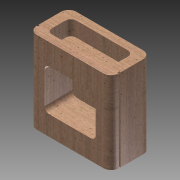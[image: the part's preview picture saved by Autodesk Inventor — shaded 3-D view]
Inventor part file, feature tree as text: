
AUTODESK INVENTOR PART (.ipt)
format: ipt  version: 2015 (Build 190159000, 159)  size: 216,576 bytes
history: native  units: in
note: dims shown in document units (in); Inventor stores cm internally (conversion verified against a paired STEP export)
features: extrude x4, sketch x4, fillet x2
ambient origin geometry x8: Origin, YZ Plane, XZ Plane, XY Plane, X Axis, Y Axis, Z Axis, Center Point
bodies: Solid1 (feature_tree)
feature tree (10):
  extrude  "Extrusion1"  Depth=1.53in
  extrude  "Extrusion2"  Depth=2.4in
  extrude  "Extrusion3"  Depth=0.57in TaperAngle=0.0deg
  extrude  "Extrusion4"  Depth=2.5in
  fillet  "Fillet1"  Radius=1.0in
  fillet  "Fillet2"  Radius=0.57in
  sketch  "Sketch1"  dims[d0=3.17in d1=1.53in]
  sketch  "Sketch2"  dims[d2=3.17in d3=0.0in d4=2.4in]
  sketch  "Sketch3"  dims[d5=0.93in d7=0.57in d8=0.0in]
  sketch  "Sketch4"  dims[d9=0.2in d10=2.5in d11=1.0in d12=0.57in d13=0.0in d14=0.3in d15=0.82in d16=1.59in d17=1.975in d18=1.07in d19=0.0in d20=0.06in d21=0.3in d23=0.01in]
